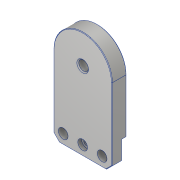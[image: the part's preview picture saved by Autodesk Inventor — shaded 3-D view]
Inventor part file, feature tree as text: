
AUTODESK INVENTOR PART (.ipt)
format: ipt  version: 2018.2 (Build 222227000, 227)  size: 246,272 bytes
history: native  units: mm
features: sketch x5, other x4, chamfer x3, extrude x2, hole x2
ambient origin geometry x8: Origin, YZ Plane, XZ Plane, XY Plane, X Axis, Y Axis, Z Axis, Center Point
bodies: Body1 (feature_tree), Body2 (feature_tree)
feature tree (16):
  other  "200-30-ROCKER-BOGIE-BEARING-01.ipt"
  extrude  "Grundkörper"  Depth=10.0mm
  hole  "BOH_D10"  [1 undecoded]
  hole  "BOH_DIN7984_M5"  [1 undecoded]
  extrude  "Absatz"  Depth=40.0mm
  chamfer  "FaseBoh"  Distance=1.0mm Angle=45.0deg
  chamfer  "FaseAbsatz"  Distance=5.0mm
  chamfer  "FaseAllgemein"  Distance=6.0mm Angle=45.0deg
  sketch  "SkizzeAbsatz"  dims[d13=60.0mm d14=10.0mm d15=6.0mm d16=10.0mm d17=5.0mm d18=90.0deg d19=8.0mm d20=20.594885mm d24=1.0mm d25=2.0mm d26=45.0deg d30=5.0mm d31=0.0mm d32=6.0mm d33=2.0mm d34=45.0deg d35=0.5mm d36=2.0mm d37=45.0deg d38=5.0mm d39=5.0mm d40=20.0mm d41=5.5mm d42=6.0mm d43=10.0mm d44=3.9mm d45=90.0deg d46=8.0mm d47=20.594885mm]
  other  "Bezeichnung3"
  sketch  "Skizze1"  dims[d2=10.0mm d3=10.0mm]
  sketch  "Skizze2"  dims[d4=5.0mm d5=25.0mm]
  sketch  "Skizze6"  dims[d8=60.0mm d9=15.0mm d10=0.0mm]
  sketch  "Skizze8"  dims[d11=10.0mm d12=40.0mm]
  other  "Volumenkörper3::200-30-ROCKER-BOGIE-BEARING-01.ipt"
  other  "Flä2"
note: 2 required parameter values undecoded (feature->parameter linkage not recoverable at this tier; creation-order binding heuristic only, values carry confidence <= 0.55)
